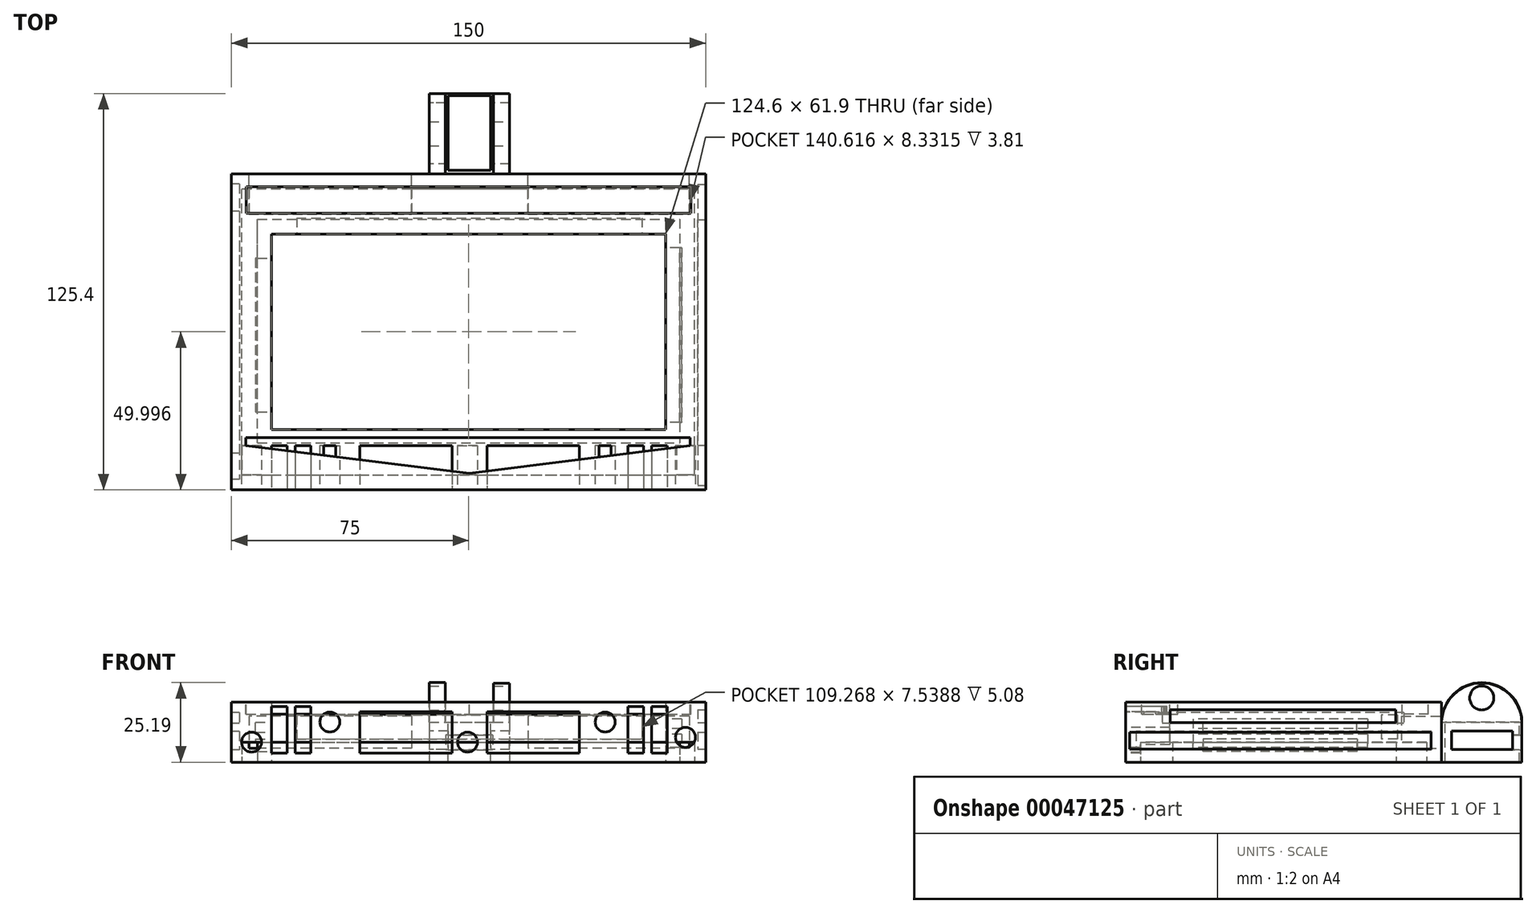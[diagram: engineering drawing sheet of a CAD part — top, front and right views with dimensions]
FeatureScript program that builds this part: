
annotation { "Feature Type Name" : "Feature", "Feature Type Description" : "" }
export const myFeature = defineFeature(function(context is Context, id is Id, definition is map)
    precondition{}
    {
        {
            var Q0;
            Q0=qCreatedBy(makeId("Top.planeOp"),FACE);
            var sketch = newSketch(context, id + "F0", { "sketchPlane" : qUnion([Q0])});
            skPoint(sketch, "E0.rect.middle", {"position": v(-0.3, -0.1) * mm});
            skLineSegment(sketch, "E1", {"start": v(-75.3, -50.1) * mm, "end": v(74.7, -50.1) * mm});
            skLineSegment(sketch, "E2", {"start": v(-75.3, 49.9) * mm, "end": v(74.7, 49.9) * mm});
            skLineSegment(sketch, "E3", {"start": v(-42.66, -50.1) * mm, "end": v(-75.3, -50.1) * mm});
            skLineSegment(sketch, "E4", {"start": v(-75.3, 49.9) * mm, "end": v(-75.3, -50.1) * mm});
            skLineSegment(sketch, "E5", {"start": v(-75.3, 49.9) * mm, "end": v(-50.44, 49.9) * mm});
            skLineSegment(sketch, "E6", {"start": v(74.7, -50.1) * mm, "end": v(74.7, 49.9) * mm});
            skLineSegment(sketch, "E0.rect.bottom", {"start": v(-62.6, 30.86) * mm, "end": v(62, 30.86) * mm});
            skLineSegment(sketch, "E0.rect.top", {"start": v(-62.6, -31.04) * mm, "end": v(62, -31.04) * mm});
            skLineSegment(sketch, "E0.rect.left", {"start": v(-62.6, 30.86) * mm, "end": v(-62.6, -31.04) * mm});
            skLineSegment(sketch, "E0.rect.right", {"start": v(62, 30.86) * mm, "end": v(62, -31.04) * mm});
            skLineSegment(sketch, "E7", {"start": v(74.7, -50.1) * mm, "end": v(67.62, -50.1) * mm});
            skLineSegment(sketch, "E8", {"start": v(-0.3, 49.9) * mm, "end": v(-25.81, 49.9) * mm});
            skSolve(sketch);
        }
        {
            var Q0;
            Q0 = qSketchRegion(id + "F0", true);
            extrude(context, id + "F1", {"entities" : qUnion([Q0]), "depth" : 19.05 * mm});
        }
        {
            var Q0;
            Q0=makeQuery(id+"F1.opExtrude","SWEPT_FACE",FACE,{"disambiguationData":[OSD([sQuery(id+"F0.wireOp",EDGE,"E1"),sQuery(id+"F0.wireOp",EDGE,"E3"),sQuery(id+"F0.wireOp",EDGE,"E7")])]});
            var sketch = newSketch(context, id + "F2", { "sketchPlane" : qUnion([Q0])});
            skLineSegment(sketch, "E9.bottom", {"start": v(-34.77, 15.96) * mm, "end": v(-5.52, 15.96) * mm});
            skLineSegment(sketch, "E9.top", {"start": v(-34.77, 2.92) * mm, "end": v(-5.52, 2.92) * mm});
            skLineSegment(sketch, "E9.left", {"start": v(-34.77, 15.96) * mm, "end": v(-34.77, 2.92) * mm});
            skLineSegment(sketch, "E9.right", {"start": v(-5.52, 15.96) * mm, "end": v(-5.52, 2.92) * mm});
            skLineSegment(sketch, "E10.bottom", {"start": v(5.6, 15.96) * mm, "end": v(34.77, 15.96) * mm});
            skLineSegment(sketch, "E10.top", {"start": v(5.6, 2.92) * mm, "end": v(34.77, 2.92) * mm});
            skLineSegment(sketch, "E10.left", {"start": v(5.6, 15.96) * mm, "end": v(5.6, 2.92) * mm});
            skLineSegment(sketch, "E10.right", {"start": v(34.77, 15.96) * mm, "end": v(34.77, 2.92) * mm});
            skLineSegment(sketch, "E11.bottom", {"start": v(-62.62, 17.55) * mm, "end": v(-57.67, 17.55) * mm});
            skLineSegment(sketch, "E11.top", {"start": v(-62.62, 2.92) * mm, "end": v(-57.67, 2.92) * mm});
            skLineSegment(sketch, "E11.left", {"start": v(-62.62, 17.55) * mm, "end": v(-62.62, 2.92) * mm});
            skLineSegment(sketch, "E11.right", {"start": v(-57.67, 17.55) * mm, "end": v(-57.67, 2.92) * mm});
            skLineSegment(sketch, "E12.bottom", {"start": v(-55.13, 17.55) * mm, "end": v(-50.17, 17.55) * mm});
            skLineSegment(sketch, "E12.top", {"start": v(-55.13, 2.92) * mm, "end": v(-50.17, 2.92) * mm});
            skLineSegment(sketch, "E12.left", {"start": v(-55.13, 17.55) * mm, "end": v(-55.13, 2.92) * mm});
            skLineSegment(sketch, "E12.right", {"start": v(-50.17, 17.55) * mm, "end": v(-50.17, 2.92) * mm});
            skLineSegment(sketch, "E13.bottom", {"start": v(50.16, 17.55) * mm, "end": v(55.11, 17.55) * mm});
            skLineSegment(sketch, "E13.top", {"start": v(50.16, 2.92) * mm, "end": v(55.11, 2.92) * mm});
            skLineSegment(sketch, "E13.left", {"start": v(50.16, 17.55) * mm, "end": v(50.16, 2.92) * mm});
            skLineSegment(sketch, "E13.right", {"start": v(55.11, 17.55) * mm, "end": v(55.11, 2.92) * mm});
            skLineSegment(sketch, "E14.bottom", {"start": v(57.65, 17.55) * mm, "end": v(62.6, 17.55) * mm});
            skLineSegment(sketch, "E14.top", {"start": v(57.65, 2.92) * mm, "end": v(62.6, 2.92) * mm});
            skLineSegment(sketch, "E14.left", {"start": v(57.65, 17.55) * mm, "end": v(57.65, 2.92) * mm});
            skLineSegment(sketch, "E14.right", {"start": v(62.6, 17.55) * mm, "end": v(62.6, 2.92) * mm});
            skCircle(sketch, "E15", {"center": v(-68.94, 6.35) * mm, "radius": 3.18 * mm});
            skCircle(sketch, "E16", {"center": v(-44.18, 12.7) * mm, "radius": 3.18 * mm});
            skCircle(sketch, "E17", {"center": v(-0.61, 6.35) * mm, "radius": 3.18 * mm});
            skCircle(sketch, "E18", {"center": v(42.95, 12.7) * mm, "radius": 3.18 * mm});
            skCircle(sketch, "E19", {"center": v(68.35, 7.86) * mm, "radius": 3.18 * mm});
            skSolve(sketch);
        }
        {
            var Q0;
            Q0=makeQuery(id+"F2.imprint","IMPRINT",FACE,{"disambiguationData":[TD([[makeQuery(id+"F2.imprint","IMPRINT",EDGE,{"derivedFrom":sQuery(id+"F2.wireOp",EDGE,"8a5435ca-d116-4785-aed5-bb8f2841af27")}),1.0]])]});
            var Q1;
            Q1=makeQuery(id+"F2.imprint","IMPRINT",FACE,{"disambiguationData":[TD([[makeQuery(id+"F2.imprint","IMPRINT",EDGE,{"derivedFrom":sQuery(id+"F2.wireOp",EDGE,"f15628e9-a327-4e10-9787-9e065b95d7da")}),1.0]])]});
            var Q2;
            Q2=makeQuery(id+"F2.imprint","IMPRINT",FACE,{"disambiguationData":[TD([[makeQuery(id+"F2.imprint","IMPRINT",EDGE,{"derivedFrom":sQuery(id+"F2.wireOp",EDGE,"2e38301c-99cb-4475-845b-e6e1d0f1830e")}),1.0]])]});
            var Q3;
            Q3=makeQuery(id+"F2.imprint","IMPRINT",FACE,{"disambiguationData":[TD([[makeQuery(id+"F2.imprint","IMPRINT",EDGE,{"derivedFrom":sQuery(id+"F2.wireOp",EDGE,"4e0002be-4994-494f-8642-1feb211b5580")}),1.0]])]});
            var Q4;
            Q4=makeQuery(id+"F2.imprint","IMPRINT",FACE,{"disambiguationData":[TD([[makeQuery(id+"F2.imprint","IMPRINT",EDGE,{"derivedFrom":sQuery(id+"F2.wireOp",EDGE,"81a880cb-7bfc-405f-9be5-3c1f6ff2c766")}),1.0]])]});
            var Q5;
            Q5=makeQuery(id+"F2.imprint","IMPRINT",FACE,{"disambiguationData":[TD([[makeQuery(id+"F2.imprint","IMPRINT",EDGE,{"derivedFrom":sQuery(id+"F2.wireOp",EDGE,"E11.bottom")}),-1.0]])]});
            var Q6;
            Q6=makeQuery(id+"F2.imprint","IMPRINT",FACE,{"disambiguationData":[TD([[makeQuery(id+"F2.imprint","IMPRINT",EDGE,{"derivedFrom":sQuery(id+"F2.wireOp",EDGE,"E12.bottom")}),-1.0]])]});
            var Q7;
            Q7=makeQuery(id+"F2.imprint","IMPRINT",FACE,{"disambiguationData":[TD([[makeQuery(id+"F2.imprint","IMPRINT",EDGE,{"derivedFrom":sQuery(id+"F2.wireOp",EDGE,"E9.bottom")}),-1.0]])]});
            var Q8;
            Q8=makeQuery(id+"F2.imprint","IMPRINT",FACE,{"disambiguationData":[TD([[makeQuery(id+"F2.imprint","IMPRINT",EDGE,{"derivedFrom":sQuery(id+"F2.wireOp",EDGE,"E10.bottom")}),-1.0]])]});
            var Q9;
            Q9=makeQuery(id+"F2.imprint","IMPRINT",FACE,{"disambiguationData":[TD([[makeQuery(id+"F2.imprint","IMPRINT",EDGE,{"derivedFrom":sQuery(id+"F2.wireOp",EDGE,"E13.bottom")}),-1.0]])]});
            var Q10;
            Q10=makeQuery(id+"F2.imprint","IMPRINT",FACE,{"disambiguationData":[TD([[makeQuery(id+"F2.imprint","IMPRINT",EDGE,{"derivedFrom":sQuery(id+"F2.wireOp",EDGE,"E14.bottom")}),-1.0]])]});
            var Q11;
            Q11=makeQuery(id+"F2.imprint","IMPRINT",FACE,{"disambiguationData":[TD([[makeQuery(id+"F2.imprint","IMPRINT",EDGE,{"derivedFrom":sQuery(id+"F2.wireOp",EDGE,"E16")}),1.0]])]});
            var Q12;
            Q12=makeQuery(id+"F2.imprint","IMPRINT",FACE,{"disambiguationData":[TD([[makeQuery(id+"F2.imprint","IMPRINT",EDGE,{"derivedFrom":sQuery(id+"F2.wireOp",EDGE,"E17")}),1.0]])]});
            var Q13;
            Q13=makeQuery(id+"F2.imprint","IMPRINT",FACE,{"disambiguationData":[TD([[makeQuery(id+"F2.imprint","IMPRINT",EDGE,{"derivedFrom":sQuery(id+"F2.wireOp",EDGE,"E18")}),1.0]])]});
            var Q14;
            Q14=makeQuery(id+"F2.imprint","IMPRINT",FACE,{"disambiguationData":[TD([[makeQuery(id+"F2.imprint","IMPRINT",EDGE,{"derivedFrom":sQuery(id+"F2.wireOp",EDGE,"E19")}),1.0]])]});
            var Q15;
            Q15=makeQuery(id+"F2.imprint","IMPRINT",FACE,{"disambiguationData":[TD([[makeQuery(id+"F2.imprint","IMPRINT",EDGE,{"derivedFrom":sQuery(id+"F2.wireOp",EDGE,"E15")}),1.0]])]});
            extrude(context, id + "F3", {"entities" : qUnion([Q0, Q1, Q2, Q3, Q4, Q5, Q6, Q7, Q8, Q9, Q10, Q11, Q12, Q13, Q14, Q15]), "operationType" : NewBodyOperationType.REMOVE, "oppositeDirection" : true, "depth" : 13.97 * mm});
        }
        {
            var Q0;
            Q0=makeQuery(id+"F1.opExtrude","CAP_FACE",FACE,{"disambiguationData":[OSD([sQuery(id+"F0.wireOp",EDGE,"E1"),sQuery(id+"F0.wireOp",EDGE,"E2"),sQuery(id+"F0.wireOp",EDGE,"E3"),sQuery(id+"F0.wireOp",EDGE,"E4"),sQuery(id+"F0.wireOp",EDGE,"E5"),sQuery(id+"F0.wireOp",EDGE,"E6"),sQuery(id+"F0.wireOp",EDGE,"E0.rect.bottom"),sQuery(id+"F0.wireOp",EDGE,"E0.rect.top"),sQuery(id+"F0.wireOp",EDGE,"E0.rect.left"),sQuery(id+"F0.wireOp",EDGE,"E0.rect.right"),sQuery(id+"F0.wireOp",EDGE,"E7"),sQuery(id+"F0.wireOp",EDGE,"E8")])],"isStart":true});
            var sketch = newSketch(context, id + "F4", { "sketchPlane" : qUnion([Q0])});
            skLineSegment(sketch, "E20.bottom", {"start": v(-67.04, 45.4) * mm, "end": v(66.31, 45.4) * mm});
            skLineSegment(sketch, "E20.top", {"start": v(-67.04, 35.24) * mm, "end": v(66.31, 35.24) * mm});
            skLineSegment(sketch, "E20.left", {"start": v(-67.04, 45.4) * mm, "end": v(-67.04, 35.24) * mm});
            skLineSegment(sketch, "E20.right", {"start": v(66.31, 45.4) * mm, "end": v(66.31, 35.24) * mm});
            skLineSegment(sketch, "E21.bottom", {"start": v(-67.04, 35.24) * mm, "end": v(-61.12, 35.24) * mm});
            skLineSegment(sketch, "E21.top", {"start": v(-67.04, -45.2) * mm, "end": v(-67.04, -45.2) * mm});
            skLineSegment(sketch, "E21.left", {"start": v(-67.04, 35.24) * mm, "end": v(-67.04, -45.2) * mm});
            skLineSegment(sketch, "E22.bottom", {"start": v(-67.04, -45.2) * mm, "end": v(66.45, -45.2) * mm});
            skLineSegment(sketch, "E22.top", {"start": v(-67.04, -35.53) * mm, "end": v(66.45, -35.53) * mm});
            skLineSegment(sketch, "E22.left", {"start": v(-67.04, -45.2) * mm, "end": v(-67.04, -35.53) * mm});
            skLineSegment(sketch, "E22.right", {"start": v(66.45, -45.2) * mm, "end": v(66.45, -35.53) * mm});
            skLineSegment(sketch, "E23.bottom", {"start": v(66.45, -35.53) * mm, "end": v(60.96, -35.53) * mm});
            skLineSegment(sketch, "E23.top", {"start": v(66.45, 35.24) * mm, "end": v(60.96, 35.24) * mm});
            skLineSegment(sketch, "E23.left", {"start": v(66.45, -35.53) * mm, "end": v(66.45, 35.24) * mm});
            skLineSegment(sketch, "E24", {"start": v(-67.04, 45.4) * mm, "end": v(-72, 45.4) * mm});
            skLineSegment(sketch, "E25", {"start": v(-72, 45.4) * mm, "end": v(-72, -45.2) * mm});
            skLineSegment(sketch, "E26", {"start": v(-72, -45.2) * mm, "end": v(-67.04, -45.2) * mm});
            skLineSegment(sketch, "E27", {"start": v(66.31, 45.4) * mm, "end": v(71.27, 45.4) * mm});
            skLineSegment(sketch, "E28", {"start": v(71.27, 45.4) * mm, "end": v(71.27, -45.2) * mm});
            skLineSegment(sketch, "E29", {"start": v(71.27, -45.2) * mm, "end": v(66.45, -45.2) * mm});
            skSolve(sketch);
        }
        {
            var Q0;
            Q0 = qSketchRegion(id + "F4", true);
            extrude(context, id + "F5", {"entities" : qUnion([Q0]), "operationType" : NewBodyOperationType.REMOVE, "oppositeDirection" : true, "depth" : 6.35 * mm});
        }
        {
            var Q0;
            {var subQ0=sQuery(id+"F0.wireOp",EDGE,"E1");var subQ1=sQuery(id+"F0.wireOp",EDGE,"E2");var subQ2=sQuery(id+"F0.wireOp",EDGE,"E3");var subQ3=sQuery(id+"F0.wireOp",EDGE,"E4");var subQ4=sQuery(id+"F0.wireOp",EDGE,"E5");var subQ5=sQuery(id+"F0.wireOp",EDGE,"E6");var subQ6=sQuery(id+"F0.wireOp",EDGE,"E7");var subQ7=sQuery(id+"F0.wireOp",EDGE,"E8");Q0=makeQuery(id+"F5.boolean.opBoolean","SPLIT",FACE,{"disambiguationData":[TD([makeQuery(id+"F1.opExtrude","SWEPT_FACE",FACE,{"disambiguationData":[OSD([subQ3])]})])],"derivedFrom":makeQuery(id+"F1.opExtrude","CAP_FACE",FACE,{"disambiguationData":[OSD([subQ0,subQ1,subQ2,subQ3,subQ4,subQ5,sQuery(id+"F0.wireOp",EDGE,"E0.rect.bottom"),sQuery(id+"F0.wireOp",EDGE,"E0.rect.top"),sQuery(id+"F0.wireOp",EDGE,"E0.rect.left"),sQuery(id+"F0.wireOp",EDGE,"E0.rect.right"),subQ6,subQ7])],"isStart":true})});}
            var sketch = newSketch(context, id + "F6", { "sketchPlane" : qUnion([Q0])});
            skLineSegment(sketch, "E30", {"start": v(0, -49.9) * mm, "end": v(0, -75.3) * mm});
            skLineSegment(sketch, "E31", {"start": v(0, -75.3) * mm, "end": v(12.7, -75.3) * mm});
            skLineSegment(sketch, "E32", {"start": v(12.7, -75.3) * mm, "end": v(12.7, -49.9) * mm});
            skLineSegment(sketch, "E33", {"start": v(12.7, -49.9) * mm, "end": v(-12.7, -49.9) * mm});
            skLineSegment(sketch, "E34", {"start": v(-12.7, -49.9) * mm, "end": v(-12.7, -75.3) * mm});
            skLineSegment(sketch, "E35", {"start": v(-12.7, -75.3) * mm, "end": v(0, -75.3) * mm});
            skSolve(sketch);
        }
        {
            var Q0;
            Q0 = qSketchRegion(id + "F6", true);
            extrude(context, id + "F7", {"entities" : qUnion([Q0]), "operationType" : NewBodyOperationType.ADD, "oppositeDirection" : true, "depth" : 12.7 * mm});
        }
        {
            var Q0;
            Q0=makeQuery(id+"F1.opExtrude","CAP_FACE",FACE,{"disambiguationData":[OSD([sQuery(id+"F0.wireOp",EDGE,"E1"),sQuery(id+"F0.wireOp",EDGE,"E2"),sQuery(id+"F0.wireOp",EDGE,"E3"),sQuery(id+"F0.wireOp",EDGE,"E4"),sQuery(id+"F0.wireOp",EDGE,"E5"),sQuery(id+"F0.wireOp",EDGE,"E6"),sQuery(id+"F0.wireOp",EDGE,"E0.rect.bottom"),sQuery(id+"F0.wireOp",EDGE,"E0.rect.top"),sQuery(id+"F0.wireOp",EDGE,"E0.rect.left"),sQuery(id+"F0.wireOp",EDGE,"E0.rect.right"),sQuery(id+"F0.wireOp",EDGE,"E7"),sQuery(id+"F0.wireOp",EDGE,"E8")])],"isStart":false});
            var sketch = newSketch(context, id + "F8", { "sketchPlane" : qUnion([Q0])});
            skLineSegment(sketch, "E36.bottom", {"start": v(-70.6, 45.75) * mm, "end": v(70.02, 45.75) * mm});
            skLineSegment(sketch, "E36.top", {"start": v(-70.6, 37.42) * mm, "end": v(70.02, 37.42) * mm});
            skLineSegment(sketch, "E36.left", {"start": v(-70.6, 45.75) * mm, "end": v(-70.6, 37.42) * mm});
            skLineSegment(sketch, "E36.right", {"start": v(70.02, 45.75) * mm, "end": v(70.02, 37.42) * mm});
            skLineSegment(sketch, "E37.bottom", {"start": v(-70.74, -36.12) * mm, "end": v(69.87, -36.12) * mm});
            skLineSegment(sketch, "E37.top", {"start": v(-70.74, -33.58) * mm, "end": v(69.87, -33.58) * mm});
            skLineSegment(sketch, "E37.left", {"start": v(-70.74, -36.12) * mm, "end": v(-70.74, -33.58) * mm});
            skLineSegment(sketch, "E37.right", {"start": v(69.87, -36.12) * mm, "end": v(69.87, -33.58) * mm});
            skLineSegment(sketch, "E38.bottom", {"start": v(-70.6, 37.42) * mm, "end": v(-65.64, 37.42) * mm});
            skLineSegment(sketch, "E38.top", {"start": v(-70.6, -33.58) * mm, "end": v(-65.64, -33.58) * mm});
            skLineSegment(sketch, "E38.left", {"start": v(-70.6, 37.42) * mm, "end": v(-70.6, -33.58) * mm});
            skLineSegment(sketch, "E38.right", {"start": v(-65.64, 37.42) * mm, "end": v(-65.64, -33.58) * mm});
            skLineSegment(sketch, "E39.bottom", {"start": v(70.02, 37.42) * mm, "end": v(65.07, 37.42) * mm});
            skLineSegment(sketch, "E39.top", {"start": v(70.02, -33.58) * mm, "end": v(65.07, -33.58) * mm});
            skLineSegment(sketch, "E39.left", {"start": v(70.02, 37.42) * mm, "end": v(70.02, -33.58) * mm});
            skLineSegment(sketch, "E39.right", {"start": v(65.07, 37.42) * mm, "end": v(65.07, -33.58) * mm});
            skLineSegment(sketch, "E40", {"start": v(-70.74, -36.12) * mm, "end": v(0, -44.92) * mm});
            skLineSegment(sketch, "E41", {"start": v(0, -44.92) * mm, "end": v(69.87, -36.12) * mm});
            skSolve(sketch);
        }
        {
            var Q0;
            Q0=makeQuery(id+"F8.imprint","IMPRINT",FACE,{"disambiguationData":[TD([[makeQuery(id+"F8.imprint","IMPRINT",EDGE,{"derivedFrom":sQuery(id+"F8.wireOp",EDGE,"E36.bottom")}),-1.0]])]});
            var Q1;
            Q1=makeQuery(id+"F8.imprint","IMPRINT",FACE,{"disambiguationData":[TD([[makeQuery(id+"F8.imprint","IMPRINT",EDGE,{"derivedFrom":sQuery(id+"F8.wireOp",EDGE,"E38.bottom")}),-1.0]])]});
            var Q2;
            Q2=makeQuery(id+"F8.imprint","IMPRINT",FACE,{"disambiguationData":[TD([[makeQuery(id+"F8.imprint","IMPRINT",EDGE,{"derivedFrom":sQuery(id+"F8.wireOp",EDGE,"E39.bottom")}),1.0]])]});
            var Q3;
            Q3=makeQuery(id+"F8.imprint","IMPRINT",FACE,{"disambiguationData":[TD([[makeQuery(id+"F8.imprint","IMPRINT",EDGE,{"derivedFrom":sQuery(id+"F8.wireOp",EDGE,"E37.bottom")}),1.0]])]});
            var Q4;
            Q4=makeQuery(id+"F8.imprint","IMPRINT",FACE,{"disambiguationData":[TD([[makeQuery(id+"F8.imprint","IMPRINT",EDGE,{"derivedFrom":sQuery(id+"F8.wireOp",EDGE,"E37.bottom")}),-1.0]])]});
            extrude(context, id + "F9", {"entities" : qUnion([Q0, Q1, Q2, Q3, Q4]), "operationType" : NewBodyOperationType.REMOVE, "oppositeDirection" : true, "depth" : 3.8 * mm});
        }
        {
            var Q0;
            Q0=makeQuery(id+"F7.opExtrude","SWEPT_FACE",FACE,{"disambiguationData":[OSD([sQuery(id+"F6.wireOp",EDGE,"E32")])]});
            var sketch = newSketch(context, id + "F10", { "sketchPlane" : qUnion([Q0])});
            skArc(sketch, "E42", {"start": v(75.3, 12.7) * mm, "mid": v(62.6, 25.02) * mm, "end": v(49.9, 12.7) * mm});
            skCircle(sketch, "E43", {"center": v(62.6, 20.32) * mm, "radius": 3.81 * mm});
            skPoint(sketch, "E44", {"position": v(62.6, 25.02) * mm});
            skSolve(sketch);
        }
        {
            var Q0;
            Q0 = qSketchRegion(id + "F10", true);
            var Q1;
            Q1=makeQuery(id+"F10.imprint","IMPRINT",FACE,{"disambiguationData":[TD([[makeQuery(id+"F10.imprint","IMPRINT",EDGE,{"derivedFrom":sQuery(id+"F10.wireOp",EDGE,"E42")}),1.0]])]});
            extrude(context, id + "F11", {"entities" : qUnion([Q0, Q1]), "operationType" : NewBodyOperationType.ADD, "oppositeDirection" : true, "depth" : 5.08 * mm});
        }
        {
            var Q0;
            Q0=makeQuery(id+"F7.opExtrude","SWEPT_FACE",FACE,{"disambiguationData":[OSD([sQuery(id+"F6.wireOp",EDGE,"E34")])]});
            var sketch = newSketch(context, id + "F12", { "sketchPlane" : qUnion([Q0])});
            skArc(sketch, "E45", {"start": v(-49.9, 12.7) * mm, "mid": v(-62.6, 25.2) * mm, "end": v(-75.3, 12.7) * mm});
            skPoint(sketch, "E46", {"position": v(-62.6, 12.7) * mm});
            skSolve(sketch);
        }
        {
            var Q0;
            Q0 = qSketchRegion(id + "F12", true);
            var Q1;
            Q1=makeQuery(id+"F12.imprint","IMPRINT",FACE,{"disambiguationData":[TD([[makeQuery(id+"F12.imprint","IMPRINT",EDGE,{"derivedFrom":sQuery(id+"F12.wireOp",EDGE,"E45")}),1.0]])]});
            extrude(context, id + "F13", {"entities" : qUnion([Q0, Q1]), "operationType" : NewBodyOperationType.ADD, "oppositeDirection" : true, "depth" : 5.08 * mm});
        }
        {
            var Q0;
            Q0 = qSketchRegion(id + "F10", true);
            extrude(context, id + "F14", {"entities" : qUnion([Q0]), "operationType" : NewBodyOperationType.REMOVE, "oppositeDirection" : true, "depth" : 31.75 * mm});
        }
        {
            var Q0;
            Q0=makeQuery(id+"F1.opExtrude","SWEPT_FACE",FACE,{"disambiguationData":[OSD([sQuery(id+"F0.wireOp",EDGE,"E4")])]});
            var sketch = newSketch(context, id + "F15", { "sketchPlane" : qUnion([Q0])});
            skLineSegment(sketch, "E47", {"start": v(50.1, 19.05) * mm, "end": v(62.8, 19.05) * mm});
            skLineSegment(sketch, "E48", {"start": v(56.44, 19.05) * mm, "end": v(-65.44, 19.05) * mm});
            skLineSegment(sketch, "E49", {"start": v(-62.12, 19.05) * mm, "end": v(-47.15, 19.05) * mm});
            skSolve(sketch);
        }
        {
            var Q0;
            Q0=makeQuery(id+"F7.opExtrude","CAP_FACE",FACE,{"disambiguationData":[OSD([sQuery(id+"F6.wireOp",EDGE,"E31"),sQuery(id+"F6.wireOp",EDGE,"E32"),sQuery(id+"F6.wireOp",EDGE,"E33"),sQuery(id+"F6.wireOp",EDGE,"E34"),sQuery(id+"F6.wireOp",EDGE,"E35")])],"isStart":false});
            var sketch = newSketch(context, id + "F16", { "sketchPlane" : qUnion([Q0])});
            skLineSegment(sketch, "E50.bottom", {"start": v(-6.77, 74.56) * mm, "end": v(6.73, 74.56) * mm});
            skLineSegment(sketch, "E50.top", {"start": v(-6.77, 50.98) * mm, "end": v(6.73, 50.98) * mm});
            skLineSegment(sketch, "E50.left", {"start": v(-6.77, 74.56) * mm, "end": v(-6.77, 50.98) * mm});
            skLineSegment(sketch, "E50.right", {"start": v(6.73, 74.56) * mm, "end": v(6.73, 50.98) * mm});
            skSolve(sketch);
        }
        {
            var Q0;
            Q0 = qSketchRegion(id + "F16", true);
            extrude(context, id + "F17", {"entities" : qUnion([Q0]), "operationType" : NewBodyOperationType.REMOVE, "oppositeDirection" : true, "depth" : 25.4 * mm});
        }
        {
            var Q0;
            {var subQ0=sQuery(id+"F6.wireOp",EDGE,"E34");Q0=makeQuery(id+"F13.boolean.opBoolean","MERGE",FACE,{"derivedFrom":[makeQuery(id+"F7.opExtrude","SWEPT_FACE",FACE,{"disambiguationData":[OSD([subQ0])]}),makeQuery(id+"F13.opExtrude","CAP_FACE",FACE,{"disambiguationData":[OSD([subQ0,sQuery(id+"F12.wireOp",EDGE,"E45")])],"isStart":true})]});}
            var sketch = newSketch(context, id + "F18", { "sketchPlane" : qUnion([Q0])});
            skLineSegment(sketch, "E51.bottom", {"start": v(-72.34, 9.82) * mm, "end": v(-53.06, 9.82) * mm});
            skLineSegment(sketch, "E51.top", {"start": v(-72.34, 4.06) * mm, "end": v(-53.06, 4.06) * mm});
            skLineSegment(sketch, "E51.left", {"start": v(-72.34, 9.82) * mm, "end": v(-72.34, 4.06) * mm});
            skLineSegment(sketch, "E51.right", {"start": v(-53.06, 9.82) * mm, "end": v(-53.06, 4.06) * mm});
            skSolve(sketch);
        }
        {
            var Q0;
            Q0 = qSketchRegion(id + "F18", true);
            extrude(context, id + "F19", {"entities" : qUnion([Q0]), "operationType" : NewBodyOperationType.REMOVE, "oppositeDirection" : true, "depth" : 31.75 * mm});
        }
        {
            var Q0;
            Q0=makeQuery(id+"F7.opExtrude","SWEPT_FACE",FACE,{"disambiguationData":[OSD([sQuery(id+"F6.wireOp",EDGE,"E31"),sQuery(id+"F6.wireOp",EDGE,"E35")])]});
            var sketch = newSketch(context, id + "F20", { "sketchPlane" : qUnion([Q0])});
            skLineSegment(sketch, "E52.bottom", {"start": v(-7.36, 8.56) * mm, "end": v(7.57, 8.56) * mm});
            skLineSegment(sketch, "E52.top", {"start": v(-7.36, 3.85) * mm, "end": v(7.57, 3.85) * mm});
            skLineSegment(sketch, "E52.left", {"start": v(-7.36, 8.56) * mm, "end": v(-7.36, 3.85) * mm});
            skLineSegment(sketch, "E52.right", {"start": v(7.57, 8.56) * mm, "end": v(7.57, 3.85) * mm});
            skSolve(sketch);
        }
        {
            var Q0;
            Q0 = qSketchRegion(id + "F20", true);
            extrude(context, id + "F21", {"entities" : qUnion([Q0]), "operationType" : NewBodyOperationType.REMOVE, "oppositeDirection" : true, "depth" : 19.05 * mm});
        }
        {
            var Q0;
            Q0=makeQuery(id+"F1.opExtrude","SWEPT_FACE",FACE,{"disambiguationData":[OSD([sQuery(id+"F0.wireOp",EDGE,"E2"),sQuery(id+"F0.wireOp",EDGE,"E5"),sQuery(id+"F0.wireOp",EDGE,"E8")])]});
            var sketch = newSketch(context, id + "F22", { "sketchPlane" : qUnion([Q0])});
            skLineSegment(sketch, "E53.bottom", {"start": v(-69.52, 14.58) * mm, "end": v(-18.47, 14.58) * mm});
            skLineSegment(sketch, "E53.top", {"start": v(-69.52, 4.4) * mm, "end": v(-18.47, 4.4) * mm});
            skLineSegment(sketch, "E53.left", {"start": v(-69.52, 14.58) * mm, "end": v(-69.52, 4.4) * mm});
            skLineSegment(sketch, "E53.right", {"start": v(-18.47, 14.58) * mm, "end": v(-18.47, 4.4) * mm});
            skLineSegment(sketch, "E54.bottom", {"start": v(18.3, 14.58) * mm, "end": v(69.72, 14.58) * mm});
            skLineSegment(sketch, "E54.top", {"start": v(18.3, 4.4) * mm, "end": v(69.72, 4.4) * mm});
            skLineSegment(sketch, "E54.left", {"start": v(18.3, 14.58) * mm, "end": v(18.3, 4.4) * mm});
            skLineSegment(sketch, "E54.right", {"start": v(69.72, 14.58) * mm, "end": v(69.72, 4.4) * mm});
            skSolve(sketch);
        }
        {
            var Q0;
            Q0 = qSketchRegion(id + "F22", true);
            extrude(context, id + "F23", {"entities" : qUnion([Q0]), "operationType" : NewBodyOperationType.REMOVE, "oppositeDirection" : true, "depth" : 12.7 * mm});
        }
        {
            var Q0;
            {var subQ0=sQuery(id+"F0.wireOp",EDGE,"E4");Q0=makeQuery(id+"F15.imprint","IMPRINT",FACE,{"disambiguationData":[TD([[makeQuery(id+"F15.imprint","IMPRINT",EDGE,{"derivedFrom":makeQuery(id+"F1.opExtrude","CAP_EDGE",EDGE,{"disambiguationData":[OSD([subQ0])],"isStart":true})}),1.0]])]});}
            var sketch = newSketch(context, id + "F24", { "sketchPlane" : qUnion([Q0])});
            skLineSegment(sketch, "E55.bottom", {"start": v(-46.67, 9.68) * mm, "end": v(46.74, 9.68) * mm});
            skLineSegment(sketch, "E55.top", {"start": v(-46.67, 3.84) * mm, "end": v(46.74, 3.84) * mm});
            skLineSegment(sketch, "E55.left", {"start": v(-46.67, 9.68) * mm, "end": v(-46.67, 3.84) * mm});
            skLineSegment(sketch, "E55.right", {"start": v(46.74, 9.68) * mm, "end": v(46.74, 3.84) * mm});
            skLineSegment(sketch, "E56.bottom", {"start": v(-37.98, 15.7) * mm, "end": v(38.49, 15.7) * mm});
            skLineSegment(sketch, "E56.top", {"start": v(-37.98, 12.26) * mm, "end": v(38.49, 12.26) * mm});
            skLineSegment(sketch, "E56.left", {"start": v(-37.98, 15.7) * mm, "end": v(-37.98, 12.26) * mm});
            skLineSegment(sketch, "E56.right", {"start": v(38.49, 15.7) * mm, "end": v(38.49, 12.26) * mm});
            skSolve(sketch);
        }
        {
            var Q0;
            Q0 = qSketchRegion(id + "F24", true);
            extrude(context, id + "F25", {"entities" : qUnion([Q0]), "operationType" : NewBodyOperationType.REMOVE, "oppositeDirection" : true, "depth" : 2.54 * mm});
        }
        {
            var Q0;
            Q0=makeQuery(id+"F1.opExtrude","SWEPT_FACE",FACE,{"disambiguationData":[OSD([sQuery(id+"F0.wireOp",EDGE,"E6")])]});
            var sketch = newSketch(context, id + "F26", { "sketchPlane" : qUnion([Q0])});
            skPoint(sketch, "E57.firstSnap0", {"position": v(49.9, 9.53) * mm});
            skLineSegment(sketch, "E57.bottom", {"start": v(46.57, 9.53) * mm, "end": v(-48.75, 9.53) * mm});
            skLineSegment(sketch, "E57.top", {"start": v(46.57, 4.1) * mm, "end": v(-48.75, 4.1) * mm});
            skLineSegment(sketch, "E57.left", {"start": v(46.57, 9.53) * mm, "end": v(46.57, 4.1) * mm});
            skLineSegment(sketch, "E57.right", {"start": v(-48.75, 9.53) * mm, "end": v(-48.75, 4.1) * mm});
            skLineSegment(sketch, "E58.bottom", {"start": v(-35.99, 16.6) * mm, "end": v(35.4, 16.6) * mm});
            skLineSegment(sketch, "E58.top", {"start": v(-35.99, 12.52) * mm, "end": v(35.4, 12.52) * mm});
            skLineSegment(sketch, "E58.left", {"start": v(-35.99, 16.6) * mm, "end": v(-35.99, 12.52) * mm});
            skLineSegment(sketch, "E58.right", {"start": v(35.4, 16.6) * mm, "end": v(35.4, 12.52) * mm});
            skSolve(sketch);
        }
        {
            var Q0;
            Q0 = qSketchRegion(id + "F26", true);
            extrude(context, id + "F27", {"entities" : qUnion([Q0]), "operationType" : NewBodyOperationType.REMOVE, "oppositeDirection" : true, "depth" : 2.54 * mm});
        }
        {
            var Q0;
            Q0=makeQuery(id+"F1.opExtrude","SWEPT_FACE",FACE,{"disambiguationData":[OSD([sQuery(id+"F0.wireOp",EDGE,"E0.rect.bottom")])]});
            var sketch = newSketch(context, id + "F28", { "sketchPlane" : qUnion([Q0])});
            skLineSegment(sketch, "E59.bottom", {"start": v(-54.67, 14.9) * mm, "end": v(54.6, 14.9) * mm});
            skLineSegment(sketch, "E59.top", {"start": v(-54.67, 7.35) * mm, "end": v(54.6, 7.35) * mm});
            skLineSegment(sketch, "E59.left", {"start": v(-54.67, 14.9) * mm, "end": v(-54.67, 7.35) * mm});
            skLineSegment(sketch, "E59.right", {"start": v(54.6, 14.9) * mm, "end": v(54.6, 7.35) * mm});
            skSolve(sketch);
        }
        {
            var Q0;
            Q0 = qSketchRegion(id + "F28", true);
            extrude(context, id + "F29", {"entities" : qUnion([Q0]), "operationType" : NewBodyOperationType.REMOVE, "oppositeDirection" : true, "depth" : 5.08 * mm});
        }
        {
            var Q0;
            Q0=makeQuery(id+"F1.opExtrude","SWEPT_FACE",FACE,{"disambiguationData":[OSD([sQuery(id+"F0.wireOp",EDGE,"E0.rect.left")])]});
            var sketch = newSketch(context, id + "F30", { "sketchPlane" : qUnion([Q0])});
            skPoint(sketch, "E60.firstSnap0", {"position": v(-31.04, 9.53) * mm});
            skLineSegment(sketch, "E60.bottom", {"start": v(23.14, 9.53) * mm, "end": v(-25.51, 9.53) * mm});
            skLineSegment(sketch, "E60.top", {"start": v(23.14, 12.7) * mm, "end": v(-25.51, 12.7) * mm});
            skLineSegment(sketch, "E60.left", {"start": v(23.14, 9.53) * mm, "end": v(23.14, 12.7) * mm});
            skLineSegment(sketch, "E60.right", {"start": v(-25.51, 9.53) * mm, "end": v(-25.51, 12.7) * mm});
            skLineSegment(sketch, "E61.bottom", {"start": v(23.18, 7.27) * mm, "end": v(-25.51, 7.27) * mm});
            skLineSegment(sketch, "E61.top", {"start": v(23.18, 3.35) * mm, "end": v(-25.51, 3.35) * mm});
            skLineSegment(sketch, "E61.left", {"start": v(23.18, 7.27) * mm, "end": v(23.18, 3.35) * mm});
            skLineSegment(sketch, "E61.right", {"start": v(-25.51, 7.27) * mm, "end": v(-25.51, 3.35) * mm});
            skSolve(sketch);
        }
        {
            var Q0;
            Q0 = qSketchRegion(id + "F30", true);
            extrude(context, id + "F31", {"entities" : qUnion([Q0]), "operationType" : NewBodyOperationType.REMOVE, "oppositeDirection" : true, "depth" : 5.08 * mm});
        }
        {
            var Q0;
            Q0=makeQuery(id+"F1.opExtrude","SWEPT_FACE",FACE,{"disambiguationData":[OSD([sQuery(id+"F0.wireOp",EDGE,"E0.rect.right")])]});
            var sketch = newSketch(context, id + "F32", { "sketchPlane" : qUnion([Q0])});
            skLineSegment(sketch, "E62.bottom", {"start": v(-26.52, 8.78) * mm, "end": v(28.77, 8.78) * mm});
            skLineSegment(sketch, "E62.top", {"start": v(-26.52, 4.7) * mm, "end": v(28.77, 4.7) * mm});
            skLineSegment(sketch, "E62.left", {"start": v(-26.52, 8.78) * mm, "end": v(-26.52, 4.7) * mm});
            skLineSegment(sketch, "E62.right", {"start": v(28.77, 8.78) * mm, "end": v(28.77, 4.7) * mm});
            skLineSegment(sketch, "E63.bottom", {"start": v(-26.5, 13.68) * mm, "end": v(28.8, 13.68) * mm});
            skLineSegment(sketch, "E63.top", {"start": v(-26.5, 10.6) * mm, "end": v(28.8, 10.6) * mm});
            skLineSegment(sketch, "E63.left", {"start": v(-26.5, 13.68) * mm, "end": v(-26.5, 10.6) * mm});
            skLineSegment(sketch, "E63.right", {"start": v(28.8, 13.68) * mm, "end": v(28.8, 10.6) * mm});
            skSolve(sketch);
        }
        {
            var Q0;
            Q0 = qSketchRegion(id + "F32", true);
            extrude(context, id + "F33", {"entities" : qUnion([Q0]), "operationType" : NewBodyOperationType.REMOVE, "oppositeDirection" : true, "depth" : 5.08 * mm});
        }
    });
